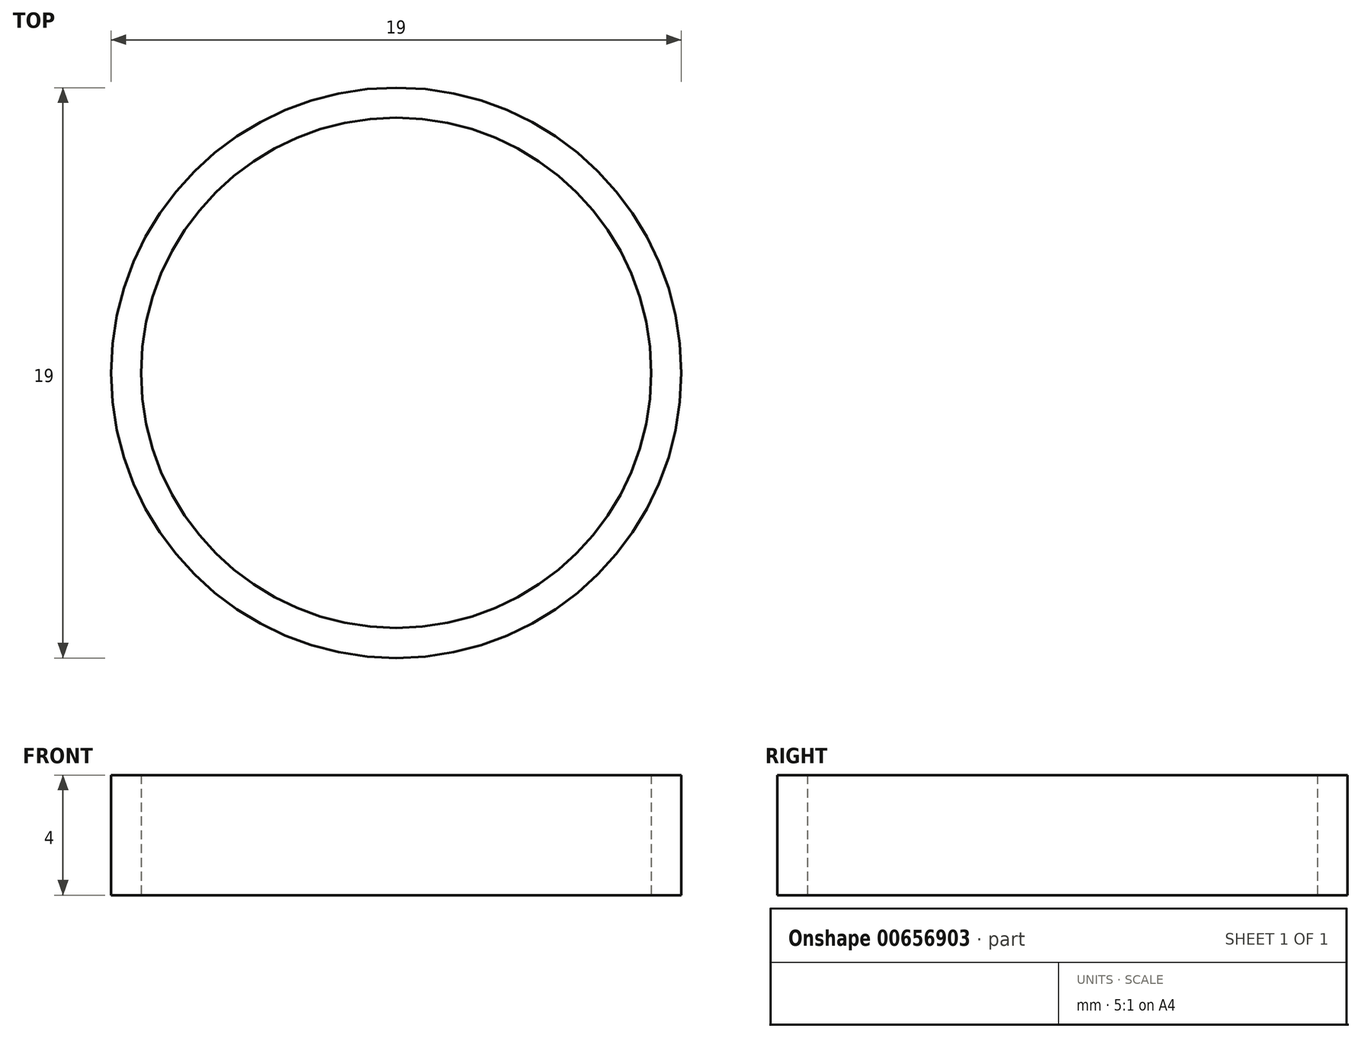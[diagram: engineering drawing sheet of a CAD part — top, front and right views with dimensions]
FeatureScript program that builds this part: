
annotation { "Feature Type Name" : "Feature", "Feature Type Description" : "" }
export const myFeature = defineFeature(function(context is Context, id is Id, definition is map)
    precondition{}
    {
        {
            var Q0;
            Q0=qCreatedBy(makeId("Top.planeOp"),FACE);
            var sketch = newSketch(context, id + "F0", { "sketchPlane" : qUnion([Q0])});
            skCircle(sketch, "E0", {"center": v(0, 0) * mm, "radius": 9.5 * mm});
            skCircle(sketch, "E1", {"center": v(0, 0) * mm, "radius": 8.5 * mm});
            skSolve(sketch);
        }
        {
            var Q0;
            Q0 = qSketchRegion(id + "F0", true);
            extrude(context, id + "F1", {"entities" : qUnion([Q0]), "endBound" : BoundingType.SYMMETRIC, "depth" : 4 * mm, "offsetDistance" : 25 * mm});
        }
    });
